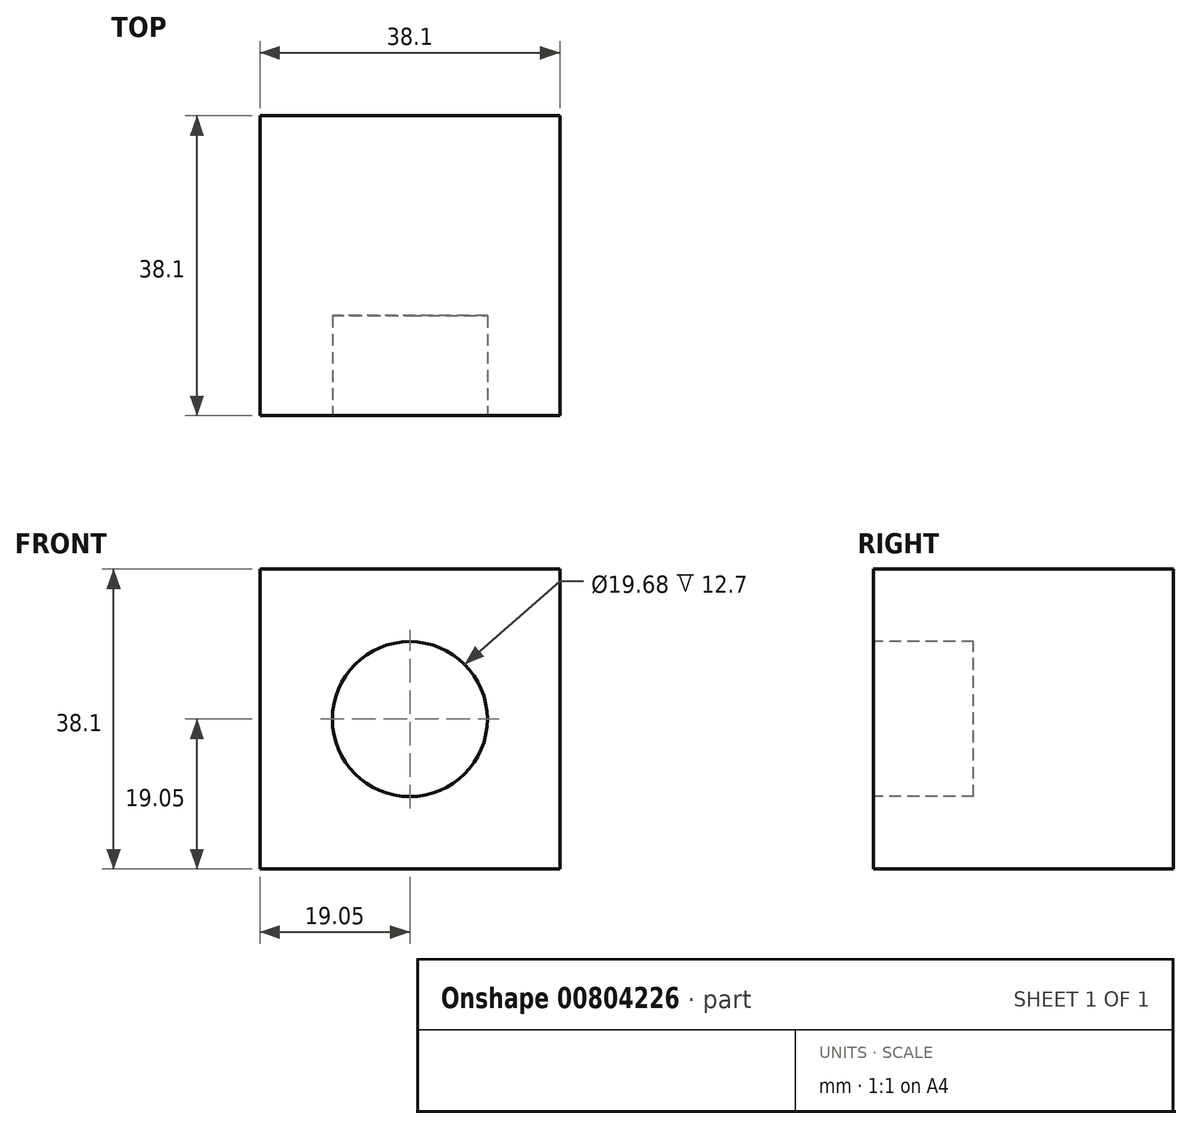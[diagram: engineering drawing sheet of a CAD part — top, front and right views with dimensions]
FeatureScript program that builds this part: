
annotation { "Feature Type Name" : "Feature", "Feature Type Description" : "" }
export const myFeature = defineFeature(function(context is Context, id is Id, definition is map)
    precondition{}
    {
        {
            var Q0;
            Q0=qCreatedBy(makeId("Front.planeOp"),FACE);
            var sketch = newSketch(context, id + "F0", { "sketchPlane" : qUnion([Q0])});
            skLineSegment(sketch, "E0", {"start": v(0, 0) * mm, "end": v(38.1, 0) * mm});
            skLineSegment(sketch, "E1", {"start": v(38.1, 0) * mm, "end": v(38.1, 38.1) * mm});
            skLineSegment(sketch, "E2", {"start": v(38.1, 38.1) * mm, "end": v(0, 38.1) * mm});
            skLineSegment(sketch, "E3", {"start": v(0, 38.1) * mm, "end": v(0, 0) * mm});
            skSolve(sketch);
        }
        {
            var Q0;
            Q0=makeQuery(id+"F0.imprint","IMPRINT",FACE,{"disambiguationData":[TD([[makeQuery(id+"F0.imprint","IMPRINT",EDGE,{"derivedFrom":sQuery(id+"F0.wireOp",EDGE,"E0")}),1.0]])]});
            extrude(context, id + "F1", {"entities" : qUnion([Q0]), "depth" : 38.1 * mm, "offsetDistance" : 25.4 * mm});
        }
        {
            var Q0;
            Q0=makeQuery(id+"F1.opExtrude","CAP_FACE",FACE,{"disambiguationData":[OSD([sQuery(id+"F0.wireOp",EDGE,"E0"),sQuery(id+"F0.wireOp",EDGE,"E1"),sQuery(id+"F0.wireOp",EDGE,"E2"),sQuery(id+"F0.wireOp",EDGE,"E3")])],"isStart":false});
            var sketch = newSketch(context, id + "F2", { "sketchPlane" : qUnion([Q0])});
            skLineSegment(sketch, "E4", {"start": v(0, 38.1) * mm, "end": v(0, 19.05) * mm, "construction": true});
            skLineSegment(sketch, "E5", {"start": v(0, 19.05) * mm, "end": v(19.05, 19.05) * mm, "construction": true});
            skCircle(sketch, "E6", {"center": v(19.05, 19.05) * mm, "radius": 9.84 * mm});
            skSolve(sketch);
        }
        {
            var Q0;
            Q0=makeQuery(id+"F2.imprint","IMPRINT",FACE,{"disambiguationData":[TD([[makeQuery(id+"F2.imprint","IMPRINT",EDGE,{"derivedFrom":sQuery(id+"F2.wireOp",EDGE,"E6")}),1.0]])]});
            extrude(context, id + "F3", {"entities" : qUnion([Q0]), "operationType" : NewBodyOperationType.REMOVE, "oppositeDirection" : true, "depth" : 12.7 * mm, "offsetDistance" : 25.4 * mm});
        }
    });
